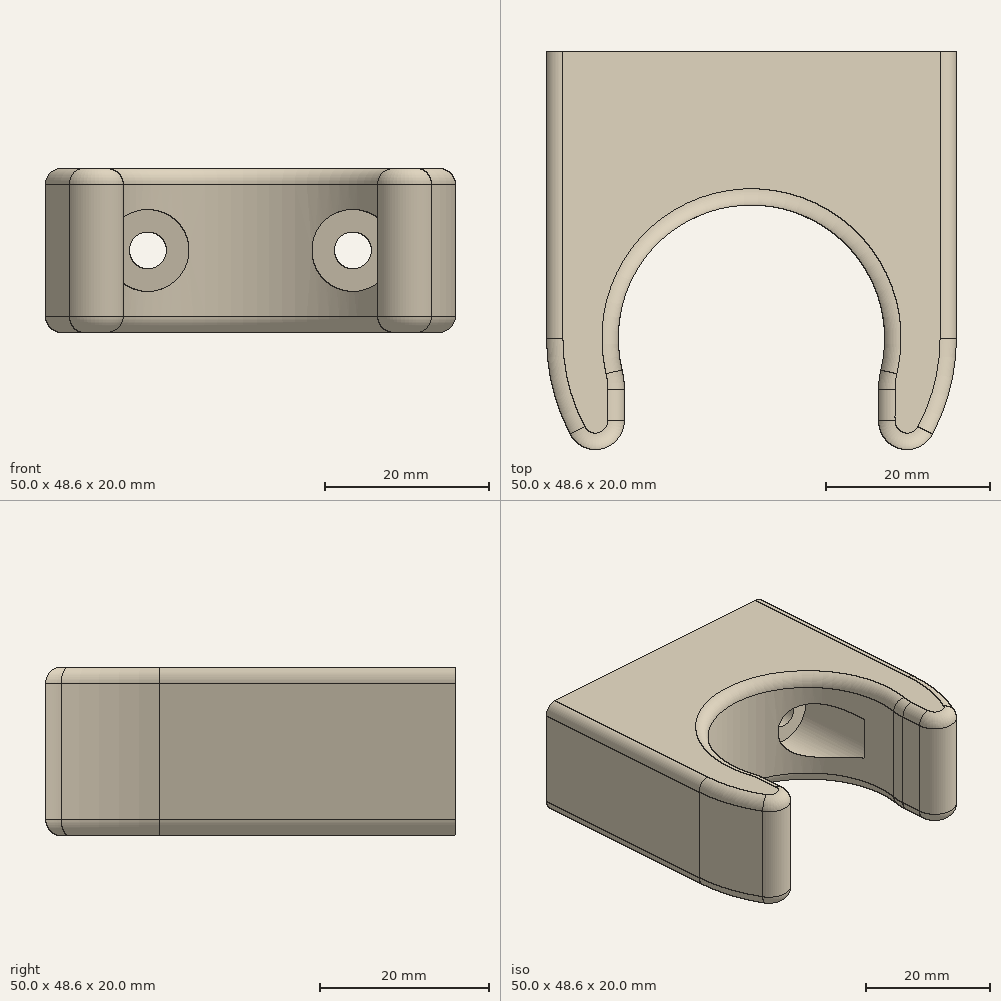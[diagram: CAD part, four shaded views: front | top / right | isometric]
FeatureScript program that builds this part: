
annotation { "Feature Type Name" : "Feature", "Feature Type Description" : "" }
export const myFeature = defineFeature(function(context is Context, id is Id, definition is map)
    precondition{}
    {
        {
            var Q0;
            Q0=qCreatedBy(makeId("Top.planeOp"),FACE);
            var sketch = newSketch(context, id + "F0", { "sketchPlane" : qUnion([Q0])});
            skArc(sketch, "E0", {"start": v(15.79, -3.86) * mm, "mid": v(0, 16.25) * mm, "end": v(-15.79, -3.86) * mm});
            skArc(sketch, "E1", {"start": v(-25, 0) * mm, "mid": v(-24.26, -6.03) * mm, "end": v(-22.1, -11.7) * mm});
            skLineSegment(sketch, "E2.top", {"start": v(-25, 25) * mm, "end": v(0, 25) * mm});
            skLineSegment(sketch, "E2.left", {"start": v(-25, 0) * mm, "end": v(-25, 25) * mm});
            skLineSegment(sketch, "E3.MirrorCS", {"start": v(25, 0) * mm, "end": v(25, 25) * mm});
            skLineSegment(sketch, "E4.MirrorCS", {"start": v(25, 25) * mm, "end": v(0, 25) * mm});
            skLineSegment(sketch, "E5.bottom", {"start": v(15, -43.22) * mm, "end": v(-15, -43.22) * mm, "construction": true});
            skLineSegment(sketch, "E5.top", {"start": v(15, 43.22) * mm, "end": v(-15, 43.22) * mm, "construction": true});
            skArc(sketch, "E6.trimOffspring", {"start": v(22.1, -11.7) * mm, "mid": v(24.26, -6.03) * mm, "end": v(25, 0) * mm});
            skLineSegment(sketch, "E7", {"start": v(-15.5, -6.23) * mm, "end": v(-15.5, -10.06) * mm});
            skLineSegment(sketch, "E8", {"start": v(15.5, -6.23) * mm, "end": v(15.5, -10.06) * mm});
            skPoint(sketch, "E9.visualSharp", {"position": v(-15.5, -19.62) * mm});
            skArc(sketch, "E9.filletArc", {"start": v(-22.1, -11.7) * mm, "mid": v(-18.16, -13.46) * mm, "end": v(-15.5, -10.06) * mm});
            skPoint(sketch, "E10.visualSharp", {"position": v(15.5, -19.62) * mm});
            skArc(sketch, "E10.filletArc", {"start": v(15.5, -10.06) * mm, "mid": v(18.16, -13.46) * mm, "end": v(22.1, -11.7) * mm});
            skPoint(sketch, "E11.visualSharp", {"position": v(-15.5, -4.88) * mm});
            skArc(sketch, "E11.filletArc", {"start": v(-15.5, -6.23) * mm, "mid": v(-15.57, -5.03) * mm, "end": v(-15.79, -3.86) * mm});
            skPoint(sketch, "E12.visualSharp", {"position": v(15.5, -4.88) * mm});
            skArc(sketch, "E12.filletArc", {"start": v(15.79, -3.86) * mm, "mid": v(15.57, -5.03) * mm, "end": v(15.5, -6.23) * mm});
            skSolve(sketch);
        }
        {
            var Q0;
            Q0=makeQuery(id+"F0.imprint","IMPRINT",FACE,{"disambiguationData":[TD([[makeQuery(id+"F0.imprint","IMPRINT",EDGE,{"derivedFrom":sQuery(id+"F0.wireOp",EDGE,"E0")}),-1.0]])]});
            extrude(context, id + "F1", {"entities" : qUnion([Q0]), "depth" : 20 * mm, "offsetDistance" : 25 * mm});
        }
        {
            var Q0;
            Q0=makeQuery(id+"F1.opExtrude","SWEPT_FACE",FACE,{"disambiguationData":[OSD([sQuery(id+"F0.wireOp",EDGE,"E2.top"),sQuery(id+"F0.wireOp",EDGE,"E4.MirrorCS")])]});
            var sketch = newSketch(context, id + "F2", { "sketchPlane" : qUnion([Q0])});
            skCircle(sketch, "E13", {"center": v(-12.5, 10) * mm, "radius": 3 * mm});
            skCircle(sketch, "E14", {"center": v(12.5, 10) * mm, "radius": 3 * mm});
            skLineSegment(sketch, "E15", {"start": v(-12.5, 10) * mm, "end": v(12.5, 10) * mm, "construction": true});
            skLineSegment(sketch, "E16", {"start": v(-12.5, 10) * mm, "end": v(-25, 10) * mm, "construction": true});
            skLineSegment(sketch, "E17", {"start": v(12.5, 10) * mm, "end": v(25, 10) * mm, "construction": true});
            skSolve(sketch);
        }
        {
            var Q0;
            Q0=sQuery(id+"F2.wireOp",VERTEX,"E15.start");
            var Q1;
            Q1=sQuery(id+"F2.wireOp",VERTEX,"E15.end");
            var Q2;
            Q2=makeQuery(id+"F1.opExtrude","SWEPT_BODY",BODY,{"disambiguationData":[OSD([sQuery(id+"F0.wireOp",EDGE,"E0"),sQuery(id+"F0.wireOp",EDGE,"E1"),sQuery(id+"F0.wireOp",EDGE,"E2.top"),sQuery(id+"F0.wireOp",EDGE,"E2.left"),sQuery(id+"F0.wireOp",EDGE,"E3.MirrorCS"),sQuery(id+"F0.wireOp",EDGE,"E4.MirrorCS"),sQuery(id+"F0.wireOp",EDGE,"E6.trimOffspring"),sQuery(id+"F0.wireOp",EDGE,"E7"),sQuery(id+"F0.wireOp",EDGE,"E8"),sQuery(id+"F0.wireOp",EDGE,"E9.filletArc"),sQuery(id+"F0.wireOp",EDGE,"E10.filletArc")])]});
            hole(context, id + "F3", {"style" : HoleStyle.SIMPLE, "endStyle" : HoleEndStyle.BLIND, "holeDiameter" : 4.5 * mm, "majorDiameter" : 4 * mm, "holeDepth" : 25 * mm, "tappedDepth" : 12 * mm, "tapClearance" : 3, "locations" : qUnion([Q0, Q1]), "scope" : qUnion([Q2]), "startStyle" : HoleStartStyle.PART});
        }
        {
            var Q0;
            Q0=qCreatedBy(makeId("Front.planeOp"),FACE);
            cPlane(context, id + "F4", {"entities" : qUnion([Q0]), "cplaneType" : CPlaneType.OFFSET, "offset" : 18 * mm, "oppositeDirection" : true, "width" : 150 * mm, "height" : 150 * mm});
        }
        {
            var Q0;
            Q0=qCreatedBy(id+"F4.planeOp",FACE);
            var sketch = newSketch(context, id + "F5", { "sketchPlane" : qUnion([Q0])});
            skCircle(sketch, "E18.0", {"center": v(-12.5, 10) * mm, "radius": 5 * mm});
            skCircle(sketch, "E19.0", {"center": v(12.5, 10) * mm, "radius": 5 * mm});
            skSolve(sketch);
        }
        {
            var Q0;
            Q0=makeQuery(id+"F1.opExtrude","CAP_EDGE",EDGE,{"disambiguationData":[OSD([sQuery(id+"F0.wireOp",EDGE,"E2.left")])],"isStart":true});
            var Q1;
            Q1=makeQuery(id+"F1.opExtrude","CAP_EDGE",EDGE,{"disambiguationData":[OSD([sQuery(id+"F0.wireOp",EDGE,"E1")])],"isStart":true});
            var Q2;
            Q2=makeQuery(id+"F1.opExtrude","CAP_EDGE",EDGE,{"disambiguationData":[OSD([sQuery(id+"F0.wireOp",EDGE,"E0")])],"isStart":true});
            var Q3;
            Q3=makeQuery(id+"F1.opExtrude","CAP_EDGE",EDGE,{"disambiguationData":[OSD([sQuery(id+"F0.wireOp",EDGE,"E10.filletArc")])],"isStart":true});
            var Q4;
            Q4=makeQuery(id+"F1.opExtrude","CAP_EDGE",EDGE,{"disambiguationData":[OSD([sQuery(id+"F0.wireOp",EDGE,"E3.MirrorCS")])],"isStart":false});
            var Q5;
            Q5=makeQuery(id+"F1.opExtrude","CAP_EDGE",EDGE,{"disambiguationData":[OSD([sQuery(id+"F0.wireOp",EDGE,"E0")])],"isStart":false});
            var Q6;
            Q6=makeQuery(id+"F1.opExtrude","CAP_EDGE",EDGE,{"disambiguationData":[OSD([sQuery(id+"F0.wireOp",EDGE,"E9.filletArc")])],"isStart":false});
            fillet(context, id + "F6", {"entities" : qUnion([Q0, Q1, Q2, Q3, Q4, Q5, Q6]), "radius" : 2 * mm, "tangentPropagation" : true, "allowEdgeOverflow" : false});
        }
        {
            var Q0;
            Q0=qSketchRegion(id+"F5",true);
            extrude(context, id + "F7", {"entities" : qUnion([Q0]), "operationType" : NewBodyOperationType.REMOVE, "depth" : 15 * mm, "offsetDistance" : 25 * mm});
        }
        {
            var Q0;
            Q0=makeQuery(id+"F1.opExtrude","SWEPT_FACE",FACE,{"disambiguationData":[OSD([sQuery(id+"F0.wireOp",EDGE,"E2.top"),sQuery(id+"F0.wireOp",EDGE,"E4.MirrorCS")])]});
            extrude(context, id + "F8", {"entities" : qUnion([Q0]), "operationType" : NewBodyOperationType.ADD, "depth" : 10 * mm, "offsetDistance" : 25 * mm});
        }
    });
